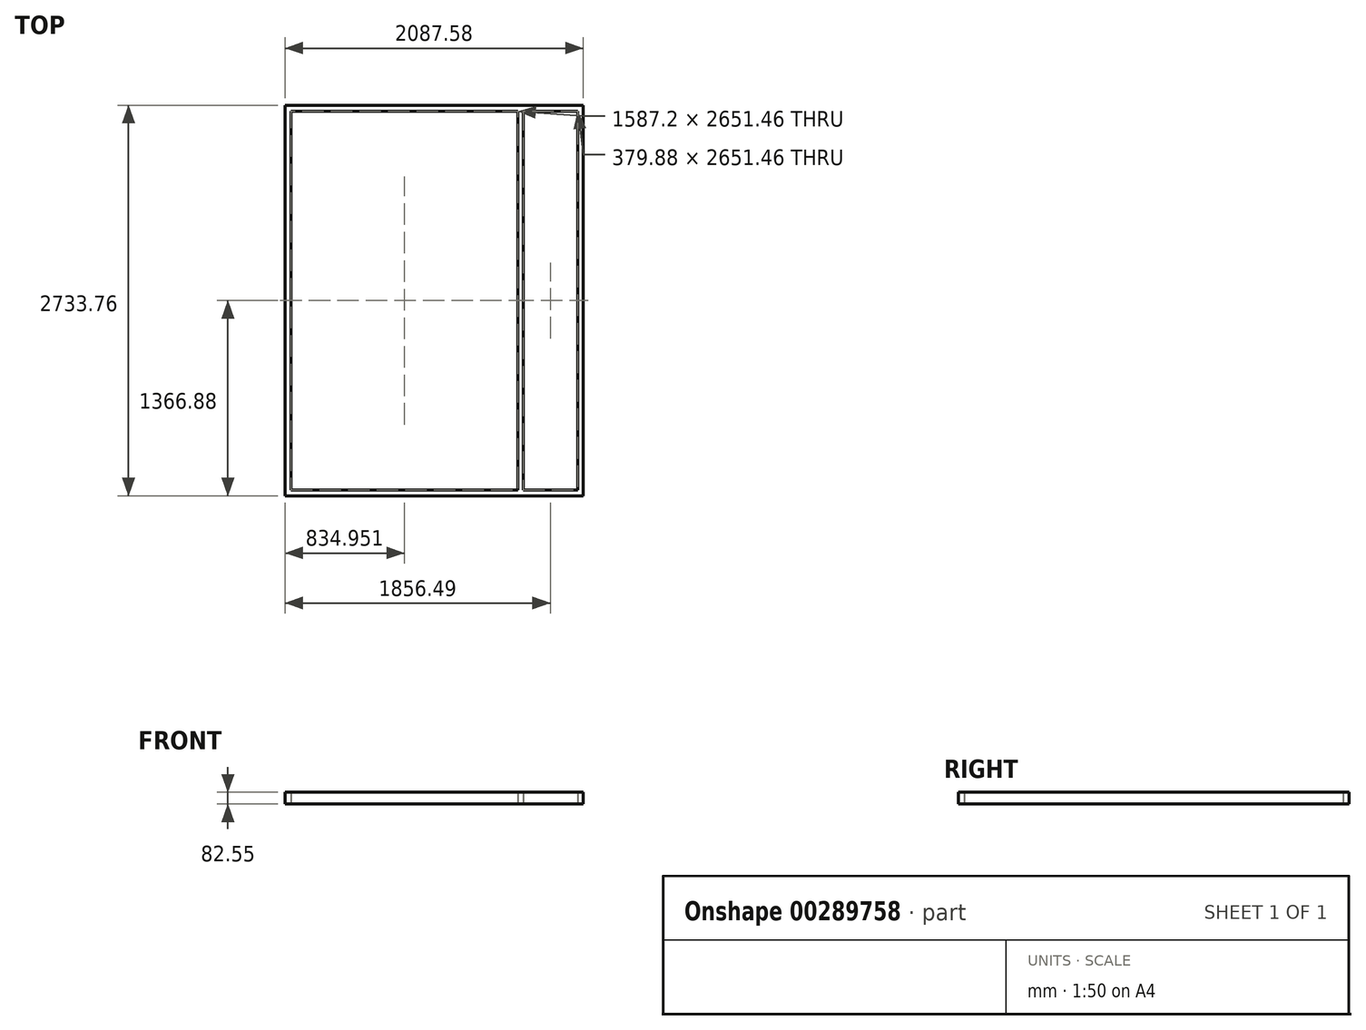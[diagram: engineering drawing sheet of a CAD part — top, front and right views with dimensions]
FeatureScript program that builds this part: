
annotation { "Feature Type Name" : "Feature", "Feature Type Description" : "" }
export const myFeature = defineFeature(function(context is Context, id is Id, definition is map)
    precondition{}
    {
        {
            var Q0;
            Q0=qCreatedBy(makeId("Top.planeOp"),FACE);
            var sketch = newSketch(context, id + "F0", { "sketchPlane" : qUnion([Q0])});
            skLineSegment(sketch, "E0.bottom", {"start": v(1043.79, -1366.88) * mm, "end": v(-1043.79, -1366.88) * mm});
            skLineSegment(sketch, "E0.top", {"start": v(1043.79, 1366.88) * mm, "end": v(-1043.79, 1366.88) * mm});
            skLineSegment(sketch, "E0.left", {"start": v(1043.79, -1366.88) * mm, "end": v(1043.79, 1366.88) * mm});
            skLineSegment(sketch, "E0.right", {"start": v(-1043.79, -1366.88) * mm, "end": v(-1043.79, 1366.88) * mm});
            skLineSegment(sketch, "E1.bottom", {"start": v(1002.64, -1325.73) * mm, "end": v(-1002.44, -1325.73) * mm});
            skLineSegment(sketch, "E1.top", {"start": v(1002.64, 1325.73) * mm, "end": v(-1002.44, 1325.73) * mm});
            skLineSegment(sketch, "E1.left", {"start": v(1002.64, -1325.73) * mm, "end": v(1002.64, 1325.73) * mm});
            skLineSegment(sketch, "E1.right", {"start": v(-1002.44, -1325.73) * mm, "end": v(-1002.44, 1325.73) * mm});
            skLineSegment(sketch, "E2.bottom", {"start": v(-230.99, 1325.73) * mm, "end": v(-189.84, 1325.73) * mm});
            skLineSegment(sketch, "E2.top", {"start": v(-230.99, -1325.73) * mm, "end": v(-189.84, -1325.73) * mm});
            skLineSegment(sketch, "E2.left", {"start": v(-230.99, 1325.73) * mm, "end": v(-230.99, -1325.73) * mm});
            skLineSegment(sketch, "E2.right", {"start": v(-189.84, 1325.73) * mm, "end": v(-189.84, -1325.73) * mm});
            skLineSegment(sketch, "E3", {"start": v(-210.41, 1325.73) * mm, "end": v(-210.41, -1325.73) * mm, "construction": true});
            skLineSegment(sketch, "E4.MirrorCS", {"start": v(584.76, 1325.73) * mm, "end": v(584.76, -1325.73) * mm});
            skLineSegment(sketch, "E5.MirrorCS", {"start": v(622.76, 1325.73) * mm, "end": v(622.76, -1325.73) * mm});
            skLineSegment(sketch, "E6.bottom", {"start": v(1002.64, 1325.73) * mm, "end": v(964.54, 1325.73) * mm});
            skLineSegment(sketch, "E6.top", {"start": v(1002.64, -1325.73) * mm, "end": v(964.54, -1325.73) * mm});
            skLineSegment(sketch, "E6.left", {"start": v(1002.64, 1325.73) * mm, "end": v(1002.64, -1325.73) * mm});
            skLineSegment(sketch, "E6.right", {"start": v(964.54, 1325.73) * mm, "end": v(964.54, -1325.73) * mm});
            skLineSegment(sketch, "E7.bottom", {"start": v(-634.24, 1325.73) * mm, "end": v(-596.14, 1325.73) * mm});
            skLineSegment(sketch, "E7.top", {"start": v(-634.24, -1325.73) * mm, "end": v(-596.14, -1325.73) * mm});
            skLineSegment(sketch, "E7.left", {"start": v(-634.24, 1325.73) * mm, "end": v(-634.24, -1325.73) * mm});
            skLineSegment(sketch, "E7.right", {"start": v(-596.14, 1325.73) * mm, "end": v(-596.14, -1325.73) * mm});
            skLineSegment(sketch, "E8.bottom", {"start": v(178.36, 1325.73) * mm, "end": v(216.46, 1325.73) * mm});
            skLineSegment(sketch, "E8.top", {"start": v(178.36, -1325.73) * mm, "end": v(216.46, -1325.73) * mm});
            skLineSegment(sketch, "E8.left", {"start": v(178.36, 1325.73) * mm, "end": v(178.36, -1325.73) * mm});
            skLineSegment(sketch, "E8.right", {"start": v(216.46, 1325.73) * mm, "end": v(216.46, -1325.73) * mm});
            skSolve(sketch);
        }
        {
            var Q0;
            {var subQ0=sQuery(id+"F0.wireOp",EDGE,"gYKtZ6Aw-8LSO-WsPd-DZTI-zDS3X9af3wS5.top");var subQ1=sQuery(id+"F0.wireOp",EDGE,"CeLBKzQn-vrWp-3Gcy-STSl-m5YtVVHxxhsw.right");var subQ2=makeQuery(id+"F0.imprint","INTERSECT",VERTEX,{"derivedFrom":[subQ1,subQ0]});Q0=makeQuery(id+"F0.imprint","IMPRINT",FACE,{"disambiguationData":[TD([[makeQuery(id+"F0.imprint","IMPRINT",EDGE,{"disambiguationData":[TD([[subQ2,1.0]])],"derivedFrom":subQ1}),1.0]])]});}
            var Q1;
            {var subQ0=sQuery(id+"F0.wireOp",EDGE,"2T1vTNZ0-FRP3-QXiO-6JWe-jevLZosKjYpy.bottom");Q1=makeQuery(id+"F0.imprint","IMPRINT",FACE,{"disambiguationData":[TD([[makeQuery(id+"F0.imprint","IMPRINT",EDGE,{"derivedFrom":subQ0}),-1.0]])]});}
            var Q2;
            {var subQ0=sQuery(id+"F0.wireOp",EDGE,"eAwVO68b-qbLe-tcLK-FJkz-neVmvZHEHzhS");Q2=makeQuery(id+"F0.imprint","IMPRINT",FACE,{"disambiguationData":[TD([[makeQuery(id+"F0.imprint","IMPRINT",EDGE,{"derivedFrom":subQ0}),1.0]])]});}
            var Q3;
            {var subQ3=sQuery(id+"F0.wireOp",EDGE,"eAwVO68b-qbLe-tcLK-FJkz-neVmvZHEHzhS");Q3=makeQuery(id+"F0.imprint","IMPRINT",FACE,{"disambiguationData":[TD([[makeQuery(id+"F0.imprint","IMPRINT",EDGE,{"derivedFrom":subQ3}),-1.0]])]});}
            var Q4;
            Q4=makeQuery(id+"F0.imprint","IMPRINT",FACE,{"disambiguationData":[TD([[makeQuery(id+"F0.imprint","IMPRINT",EDGE,{"derivedFrom":sQuery(id+"F0.wireOp",EDGE,"2T1vTNZ0-FRP3-QXiO-6JWe-jevLZosKjYpy.bottom")}),1.0]])]});
            var Q5;
            {var subQ0=sQuery(id+"F0.wireOp",EDGE,"gYKtZ6Aw-8LSO-WsPd-DZTI-zDS3X9af3wS5.top");var subQ1=sQuery(id+"F0.wireOp",EDGE,"CeLBKzQn-vrWp-3Gcy-STSl-m5YtVVHxxhsw.left");var subQ2=makeQuery(id+"F0.imprint","INTERSECT",VERTEX,{"derivedFrom":[subQ1,subQ0]});Q5=makeQuery(id+"F0.imprint","IMPRINT",FACE,{"disambiguationData":[TD([[makeQuery(id+"F0.imprint","IMPRINT",EDGE,{"disambiguationData":[TD([[subQ2,1.0]])],"derivedFrom":subQ1}),-1.0]])]});}
            var Q6;
            {var subQ5=sQuery(id+"F0.wireOp",EDGE,"RKO7VibA-5L9s-bFsq-QhT8-NU87CP0l9bWE");Q6=makeQuery(id+"F0.imprint","IMPRINT",FACE,{"disambiguationData":[TD([[makeQuery(id+"F0.imprint","IMPRINT",EDGE,{"derivedFrom":subQ5}),-1.0]])]});}
            var Q7;
            {var subQ0=sQuery(id+"F0.wireOp",EDGE,"eimdUF1S-VLgt-R7h1-7aaf-AqgagJHAWkX2");var subQ1=sQuery(id+"F0.wireOp",EDGE,"CeLBKzQn-vrWp-3Gcy-STSl-m5YtVVHxxhsw.left");var subQ2=makeQuery(id+"F0.imprint","INTERSECT",VERTEX,{"derivedFrom":[subQ1,subQ0]});Q7=makeQuery(id+"F0.imprint","IMPRINT",FACE,{"disambiguationData":[TD([[makeQuery(id+"F0.imprint","IMPRINT",EDGE,{"disambiguationData":[TD([[subQ2,-1.0]])],"derivedFrom":subQ1}),-1.0]])]});}
            var Q8;
            {var subQ0=sQuery(id+"F0.wireOp",EDGE,"gYKtZ6Aw-8LSO-WsPd-DZTI-zDS3X9af3wS5.bottom");var subQ1=sQuery(id+"F0.wireOp",EDGE,"CeLBKzQn-vrWp-3Gcy-STSl-m5YtVVHxxhsw.left");var subQ2=makeQuery(id+"F0.imprint","INTERSECT",VERTEX,{"derivedFrom":[subQ1,subQ0]});Q8=makeQuery(id+"F0.imprint","IMPRINT",FACE,{"disambiguationData":[TD([[makeQuery(id+"F0.imprint","IMPRINT",EDGE,{"disambiguationData":[TD([[subQ2,-1.0]])],"derivedFrom":subQ1}),-1.0]])]});}
            var Q9;
            {var subQ0=sQuery(id+"F0.wireOp",EDGE,"b66463a6-24de-4eea-b983-df5165fbb9630.MirrorCS");Q9=makeQuery(id+"F0.imprint","IMPRINT",FACE,{"disambiguationData":[TD([[makeQuery(id+"F0.imprint","IMPRINT",EDGE,{"derivedFrom":subQ0}),-1.0]])]});}
            var Q10;
            {var subQ0=sQuery(id+"F0.wireOp",EDGE,"E4.MirrorCS");Q10=makeQuery(id+"F0.imprint","IMPRINT",FACE,{"disambiguationData":[TD([[makeQuery(id+"F0.imprint","IMPRINT",EDGE,{"derivedFrom":subQ0}),1.0]])]});}
            var Q11;
            Q11=makeQuery(id+"F0.imprint","IMPRINT",FACE,{"disambiguationData":[TD([[makeQuery(id+"F0.imprint","IMPRINT",EDGE,{"derivedFrom":sQuery(id+"F0.wireOp",EDGE,"E2.bottom")}),-1.0]])]});
            var Q12;
            Q12=makeQuery(id+"F0.imprint","IMPRINT",FACE,{"disambiguationData":[TD([[makeQuery(id+"F0.imprint","IMPRINT",EDGE,{"derivedFrom":sQuery(id+"F0.wireOp",EDGE,"E6.bottom")}),1.0]])]});
            var Q13;
            Q13=makeQuery(id+"F0.imprint","IMPRINT",FACE,{"disambiguationData":[TD([[makeQuery(id+"F0.imprint","IMPRINT",EDGE,{"derivedFrom":sQuery(id+"F0.wireOp",EDGE,"E0.bottom")}),-1.0]])]});
            var Q14;
            Q14=makeQuery(id+"F0.imprint","IMPRINT",FACE,{"disambiguationData":[TD([[makeQuery(id+"F0.imprint","IMPRINT",EDGE,{"derivedFrom":sQuery(id+"F0.wireOp",EDGE,"E7.bottom")}),-1.0]])]});
            var Q15;
            Q15=makeQuery(id+"F0.imprint","IMPRINT",FACE,{"disambiguationData":[TD([[makeQuery(id+"F0.imprint","IMPRINT",EDGE,{"derivedFrom":sQuery(id+"F0.wireOp",EDGE,"E8.bottom")}),-1.0]])]});
            extrude(context, id + "F1", {"entities" : qUnion([Q0, Q1, Q2, Q3, Q4, Q5, Q6, Q7, Q8, Q9, Q10, Q11, Q12, Q13, Q14, Q15]), "offsetDistance" : 30.48 * mm, "depth" : 82.55 * mm});
        }
    });
